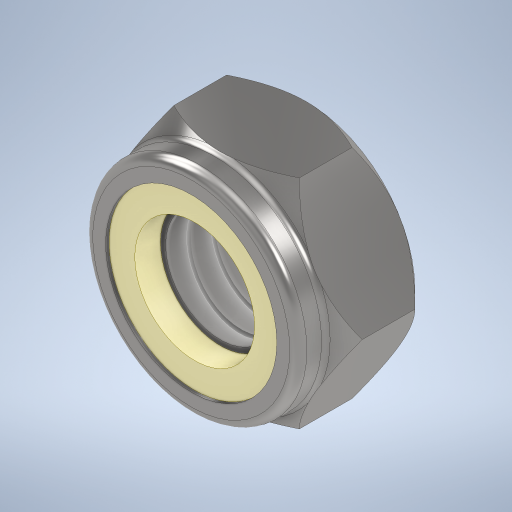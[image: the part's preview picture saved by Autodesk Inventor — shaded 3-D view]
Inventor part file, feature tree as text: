
AUTODESK INVENTOR PART (.ipt)
format: ipt  version: 2024 (Build 280153000, 153)  size: 385,024 bytes
history: native  units: mm
features: sketch x6, extrude x5, chamfer x2, hole x2, fillet x1, projected_geometry x1, other x1
ambient origin geometry x8: Origin, YZ Plane, XZ Plane, XY Plane, X Axis, Y Axis, Z Axis, Center Point
bodies: Solid1 (feature_tree)
feature tree (18):
  sketch  "Sketch1"  dims[d0=12.7mm d2=5.08mm d3=0.0mm d4=1.0mm d5=2.0mm d6=45.0deg]
  extrude  "Extrusion1"  Depth=5.08mm TaperAngle=0.0deg
  chamfer  "Chamfer1"  Distance=1.0mm Angle=45.0deg
  extrude  "Extrusion2"  Depth=12.5mm
  extrude  "Extrusion3"  Depth=0.5mm
  fillet  "Fillet1"  Radius=10.0mm
  extrude  "Extrusion4"  Depth=1.5mm TaperAngle=0.0deg
  extrude  "Extrusion5"  Depth=0.25mm TaperAngle=45.0deg
  hole  "Hole1"  [1 undecoded]
  hole  "Hole2"  [1 undecoded]
  chamfer  "Chamfer2"  [1 undecoded]
  sketch  "Sketch2"  dims[d7=0.0mm d8=0.0mm d9=12.5mm]
  sketch  "Sketch3"  dims[d10=1.651mm d11=0.0mm d12=0.5mm d13=10.0mm]
  sketch  "Sketch4"  dims[d14=1.7mm d15=0.0mm d16=1.5mm d17=0.0mm]
  projected_geometry  "Projected Loop1"
  other  "Lockring"
  sketch  "Sketch5"  dims[d18=6.4008mm d19=15.875mm d20=4.0mm d21=2.0mm d22=90.0deg d23=11.8mm d24=0.0mm]
  sketch  "Sketch6"  dims[d25=7.0mm d26=8.0mm d27=4.0mm d28=2.0mm d29=90.0deg d30=8.0mm d31=0.0mm d32=0.25mm d33=2.0mm d34=45.0deg]
note: 3 required parameter values undecoded (feature->parameter linkage not recoverable at this tier; creation-order binding heuristic only, values carry confidence <= 0.55)
